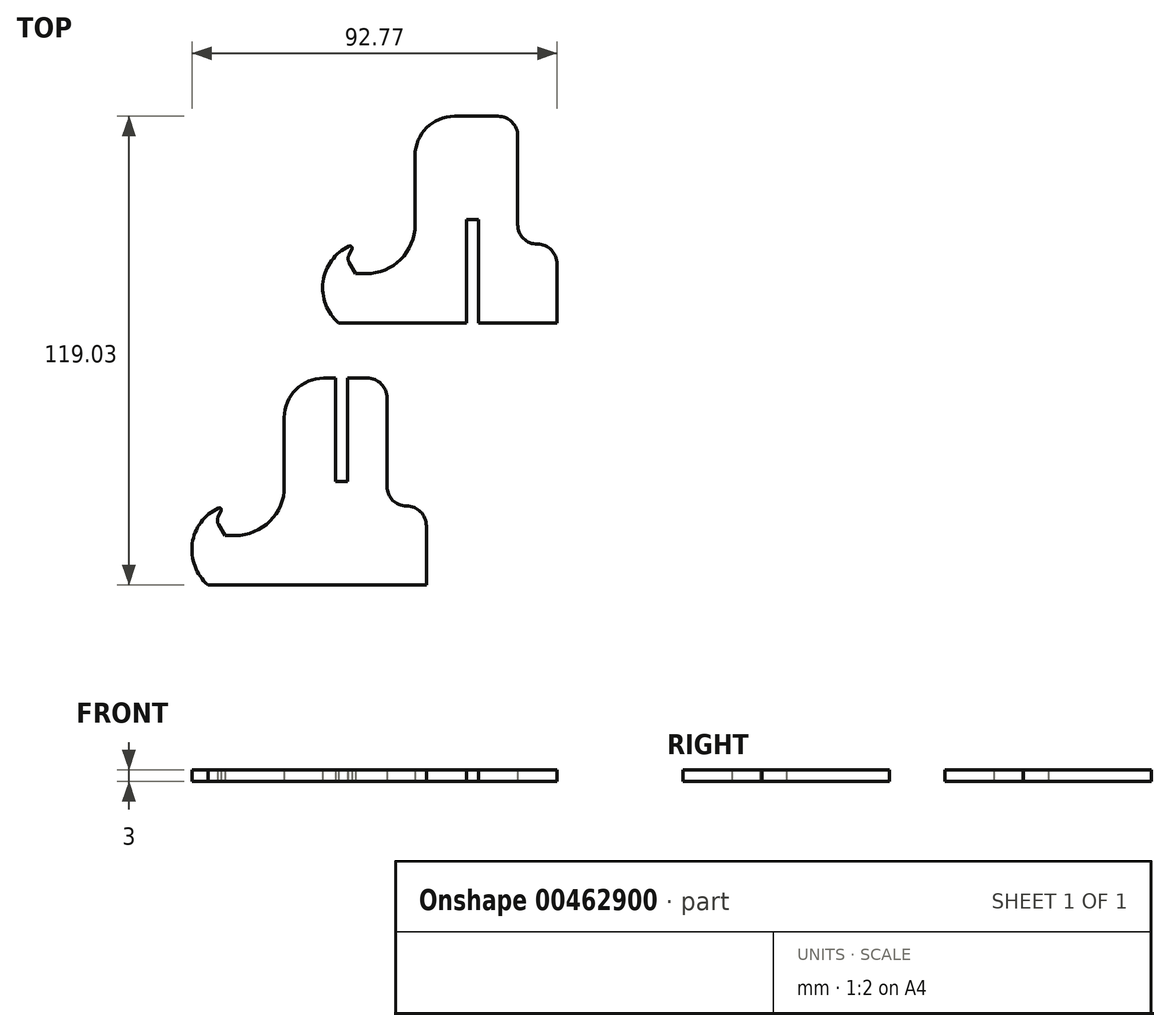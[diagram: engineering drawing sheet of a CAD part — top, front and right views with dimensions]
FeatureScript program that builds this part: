
annotation { "Feature Type Name" : "Feature", "Feature Type Description" : "" }
export const myFeature = defineFeature(function(context is Context, id is Id, definition is map)
    precondition{}
    {
        {
            var Q0;
            Q0=qCreatedBy(makeId("Top.planeOp"),FACE);
            var sketch = newSketch(context, id + "F0", { "sketchPlane" : qUnion([Q0])});
            skLineSegment(sketch, "E0", {"start": v(-16.1, 20.7) * mm, "end": v(-18.7, 20.7) * mm});
            skLineSegment(sketch, "E1", {"start": v(-18.7, 20.7) * mm, "end": v(-20.35, 23.55) * mm});
            skPoint(sketch, "E2.visualSharp", {"position": v(3.9, 50.7) * mm});
            skPoint(sketch, "E3.visualSharp", {"position": v(3.9, 20.7) * mm});
            skArc(sketch, "E3.filletArc", {"start": v(-16.1, 20.7) * mm, "mid": v(-7.26, 24.35) * mm, "end": v(-3.6, 33.2) * mm});
            skPoint(sketch, "E4.second.point", {"position": v(-27.03, 18.2) * mm});
            skPoint(sketch, "E5.orphan", {"position": v(-27.03, 28.2) * mm});
            skPoint(sketch, "E6.0.end.orphan", {"position": v(-27.03, 8.2) * mm});
            skLineSegment(sketch, "E7", {"start": v(-20.43, 25.38) * mm, "end": v(-19.67, 27.05) * mm});
            skArc(sketch, "E8", {"start": v(-20.34, 27.7) * mm, "mid": v(-26.97, 18.68) * mm, "end": v(-23.03, 8.2) * mm});
            skPoint(sketch, "E9.orphan", {"position": v(-23.03, 28.2) * mm});
            skPoint(sketch, "E10.visualSharp", {"position": v(-20.86, 24.44) * mm});
            skArc(sketch, "E10.filletArc", {"start": v(-20.43, 25.38) * mm, "mid": v(-20.61, 24.45) * mm, "end": v(-20.35, 23.55) * mm});
            skPoint(sketch, "E11.visualSharp", {"position": v(-19.14, 28.2) * mm});
            skArc(sketch, "E11.filletArc", {"start": v(-19.67, 27.05) * mm, "mid": v(-19.77, 27.61) * mm, "end": v(-20.34, 27.7) * mm});
            skLineSegment(sketch, "E12", {"start": v(-3.6, 33.2) * mm, "end": v(-3.6, 50.7) * mm});
            skPoint(sketch, "E13.visualSharp", {"position": v(-3.6, 60.7) * mm});
            skArc(sketch, "E13.filletArc", {"start": v(6.4, 60.7) * mm, "mid": v(-0.67, 57.76) * mm, "end": v(-3.6, 50.7) * mm});
            skLineSegment(sketch, "E14", {"start": v(-23.03, 8.2) * mm, "end": v(9.47, 8.2) * mm});
            skLineSegment(sketch, "E15", {"start": v(9.47, 8.2) * mm, "end": v(9.47, 34.44) * mm});
            skLineSegment(sketch, "E16", {"start": v(9.47, 34.44) * mm, "end": v(12.47, 34.44) * mm});
            skLineSegment(sketch, "E17", {"start": v(12.47, 34.44) * mm, "end": v(12.47, 8.2) * mm});
            skLineSegment(sketch, "E18", {"start": v(12.47, 8.2) * mm, "end": v(32.47, 8.2) * mm});
            skLineSegment(sketch, "E19", {"start": v(32.47, 8.2) * mm, "end": v(32.47, 23.2) * mm});
            skLineSegment(sketch, "E20", {"start": v(17.47, 60.7) * mm, "end": v(6.4, 60.7) * mm});
            skPoint(sketch, "E21.visualSharp", {"position": v(32.47, 60.7) * mm});
            skLineSegment(sketch, "E22", {"start": v(22.47, 33.2) * mm, "end": v(22.47, 55.7) * mm});
            skLineSegment(sketch, "E23", {"start": v(17.47, 60.7) * mm, "end": v(17.47, 60.7) * mm});
            skLineSegment(sketch, "E24.0", {"start": v(27.47, 28.2) * mm, "end": v(27.47, 28.2) * mm});
            skPoint(sketch, "E25.orphan", {"position": v(22.47, 8.2) * mm});
            skPoint(sketch, "E26.visualSharp", {"position": v(22.47, 60.7) * mm});
            skArc(sketch, "E26.filletArc", {"start": v(22.47, 55.7) * mm, "mid": v(21, 59.23) * mm, "end": v(17.47, 60.7) * mm});
            skPoint(sketch, "E27.visualSharp", {"position": v(22.47, 28.2) * mm});
            skArc(sketch, "E27.filletArc", {"start": v(22.47, 33.2) * mm, "mid": v(23.94, 29.66) * mm, "end": v(27.47, 28.2) * mm});
            skPoint(sketch, "E28.visualSharp", {"position": v(32.47, 28.2) * mm});
            skArc(sketch, "E28.filletArc", {"start": v(32.47, 23.2) * mm, "mid": v(31, 26.73) * mm, "end": v(27.47, 28.2) * mm});
            skLineSegment(sketch, "E29", {"start": v(-18.7, 20.7) * mm, "end": v(0.7, 62.1) * mm, "construction": true});
            skLineSegment(sketch, "E30", {"start": v(-49.32, -45.84) * mm, "end": v(-51.91, -45.84) * mm});
            skLineSegment(sketch, "E31", {"start": v(-51.91, -45.84) * mm, "end": v(-53.56, -42.99) * mm});
            skPoint(sketch, "E32.visualSharp", {"position": v(-29.32, -15.84) * mm});
            skPoint(sketch, "E33.visualSharp", {"position": v(-29.32, -45.84) * mm});
            skArc(sketch, "E33.filletArc", {"start": v(-49.32, -45.84) * mm, "mid": v(-40.48, -42.18) * mm, "end": v(-36.82, -33.34) * mm});
            skPoint(sketch, "E34.second.point", {"position": v(-60.24, -48.34) * mm});
            skPoint(sketch, "E35.orphan", {"position": v(-60.24, -38.34) * mm});
            skPoint(sketch, "E36.0.end.orphan", {"position": v(-60.24, -58.34) * mm});
            skLineSegment(sketch, "E37", {"start": v(-53.65, -41.15) * mm, "end": v(-52.88, -39.49) * mm});
            skArc(sketch, "E38", {"start": v(-53.55, -38.82) * mm, "mid": v(-60.19, -47.85) * mm, "end": v(-56.24, -58.34) * mm});
            skPoint(sketch, "E39.orphan", {"position": v(-56.24, -38.34) * mm});
            skPoint(sketch, "E40.visualSharp", {"position": v(-54.08, -42.1) * mm});
            skArc(sketch, "E40.filletArc", {"start": v(-53.65, -41.15) * mm, "mid": v(-53.83, -42.08) * mm, "end": v(-53.56, -42.99) * mm});
            skPoint(sketch, "E41.visualSharp", {"position": v(-52.36, -38.34) * mm});
            skArc(sketch, "E41.filletArc", {"start": v(-52.88, -39.49) * mm, "mid": v(-52.99, -38.92) * mm, "end": v(-53.55, -38.82) * mm});
            skLineSegment(sketch, "E42", {"start": v(-36.82, -33.34) * mm, "end": v(-36.82, -15.84) * mm});
            skPoint(sketch, "E43.visualSharp", {"position": v(-36.82, -5.84) * mm});
            skArc(sketch, "E43.filletArc", {"start": v(-26.82, -5.84) * mm, "mid": v(-33.89, -8.77) * mm, "end": v(-36.82, -15.84) * mm});
            skLineSegment(sketch, "E44", {"start": v(-56.24, -58.34) * mm, "end": v(-23.74, -58.34) * mm});
            skLineSegment(sketch, "E45", {"start": v(-23.74, -32.1) * mm, "end": v(-20.74, -32.1) * mm});
            skLineSegment(sketch, "E46", {"start": v(-20.74, -58.34) * mm, "end": v(-0.74, -58.34) * mm});
            skLineSegment(sketch, "E47", {"start": v(-0.74, -58.34) * mm, "end": v(-0.74, -43.34) * mm});
            skLineSegment(sketch, "E48", {"start": v(-15.74, -5.84) * mm, "end": v(-20.74, -5.84) * mm});
            skPoint(sketch, "E49.visualSharp", {"position": v(-0.74, -5.84) * mm});
            skLineSegment(sketch, "E50", {"start": v(-10.74, -33.34) * mm, "end": v(-10.74, -10.84) * mm});
            skLineSegment(sketch, "E51", {"start": v(-15.74, -5.84) * mm, "end": v(-15.74, -5.84) * mm});
            skLineSegment(sketch, "E52.0", {"start": v(-5.74, -38.34) * mm, "end": v(-5.74, -38.34) * mm});
            skPoint(sketch, "E53.orphan", {"position": v(-10.74, -58.34) * mm});
            skPoint(sketch, "E54.visualSharp", {"position": v(-10.74, -5.84) * mm});
            skArc(sketch, "E54.filletArc", {"start": v(-10.74, -10.84) * mm, "mid": v(-12.2, -7.3) * mm, "end": v(-15.74, -5.84) * mm});
            skPoint(sketch, "E55.visualSharp", {"position": v(-10.74, -38.34) * mm});
            skArc(sketch, "E55.filletArc", {"start": v(-10.74, -33.34) * mm, "mid": v(-9.28, -36.88) * mm, "end": v(-5.74, -38.34) * mm});
            skPoint(sketch, "E56.visualSharp", {"position": v(-0.74, -38.34) * mm});
            skArc(sketch, "E56.filletArc", {"start": v(-0.74, -43.34) * mm, "mid": v(-2.2, -39.8) * mm, "end": v(-5.74, -38.34) * mm});
            skLineSegment(sketch, "E57", {"start": v(-51.91, -45.84) * mm, "end": v(-32.52, -4.44) * mm, "construction": true});
            skLineSegment(sketch, "E58", {"start": v(-23.74, -32.1) * mm, "end": v(-23.74, -5.84) * mm});
            skLineSegment(sketch, "E59", {"start": v(-20.74, -32.1) * mm, "end": v(-20.74, -5.84) * mm});
            skLineSegment(sketch, "E60", {"start": v(-23.74, -58.34) * mm, "end": v(-20.74, -58.34) * mm});
            skLineSegment(sketch, "E61.trimOffspring", {"start": v(-23.74, -5.84) * mm, "end": v(-26.82, -5.84) * mm});
            skSolve(sketch);
        }
        {
            var Q0;
            Q0=makeQuery(id+"F0.imprint","IMPRINT",FACE,{"disambiguationData":[TD([[makeQuery(id+"F0.imprint","IMPRINT",EDGE,{"derivedFrom":sQuery(id+"F0.wireOp",EDGE,"E0")}),1.0]])]});
            var Q1;
            Q1=makeQuery(id+"F0.imprint","IMPRINT",FACE,{"disambiguationData":[TD([[makeQuery(id+"F0.imprint","IMPRINT",EDGE,{"derivedFrom":sQuery(id+"F0.wireOp",EDGE,"E30")}),1.0]])]});
            extrude(context, id + "F1", {"entities" : qUnion([Q0, Q1]), "depth" : 3 * mm});
        }
    });
